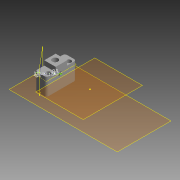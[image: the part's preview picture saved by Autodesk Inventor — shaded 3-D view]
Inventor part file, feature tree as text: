
AUTODESK INVENTOR PART (.ipt)
format: ipt  version: 2015 (Build 190159000, 159)  size: 142,336 bytes
history: native  units: mm
features: plane x4, sketch x3, reference x3, extrude x2, hole x2, fillet x1, projected_geometry x1
ambient origin geometry x8: Origin, YZ Plane, XZ Plane, XY Plane, X Axis, Y Axis, Z Axis, Center Point
bodies: Solid1 (feature_tree)
feature tree (16):
  plane  "Work Plane1"
  plane  "Work Plane2"
  extrude  "Extrusion1"  Depth=15.0mm
  plane  "Work Plane3"
  sketch  "Sketch4"  dims[d1=15.0mm d2=0.0mm d7=22.68928mm]
  plane  "Work Plane6"
  sketch  "Sketch7"  dims[d8=1.5mm d9=1.5mm]
  hole  "Hole1"  [1 undecoded]
  hole  "Hole2"  [1 undecoded]
  extrude  "Extrusion2"  Depth=2.0mm
  fillet  "Fillet1"  Radius=4.0mm
  reference  "Reference1"
  reference  "Reference2"
  reference  "Reference3"
  projected_geometry  "Projected Loop1"
  sketch  "Sketch9"  dims[d10=0.5mm d13=1.5mm d17=2.459mm d18=6.0mm d19=4.0mm d20=2.0mm d21=90.0deg d22=8.0mm d23=20.594885mm d24=2.459mm d25=6.0mm d26=4.0mm d27=2.0mm d28=90.0deg d29=8.0mm d30=20.594885mm d31=2.5mm d32=4.0mm d33=8.0mm d34=10.0mm d35=0.0mm d36=2.0mm d37=26.0mm]
note: 2 required parameter values undecoded (feature->parameter linkage not recoverable at this tier; creation-order binding heuristic only, values carry confidence <= 0.55)
